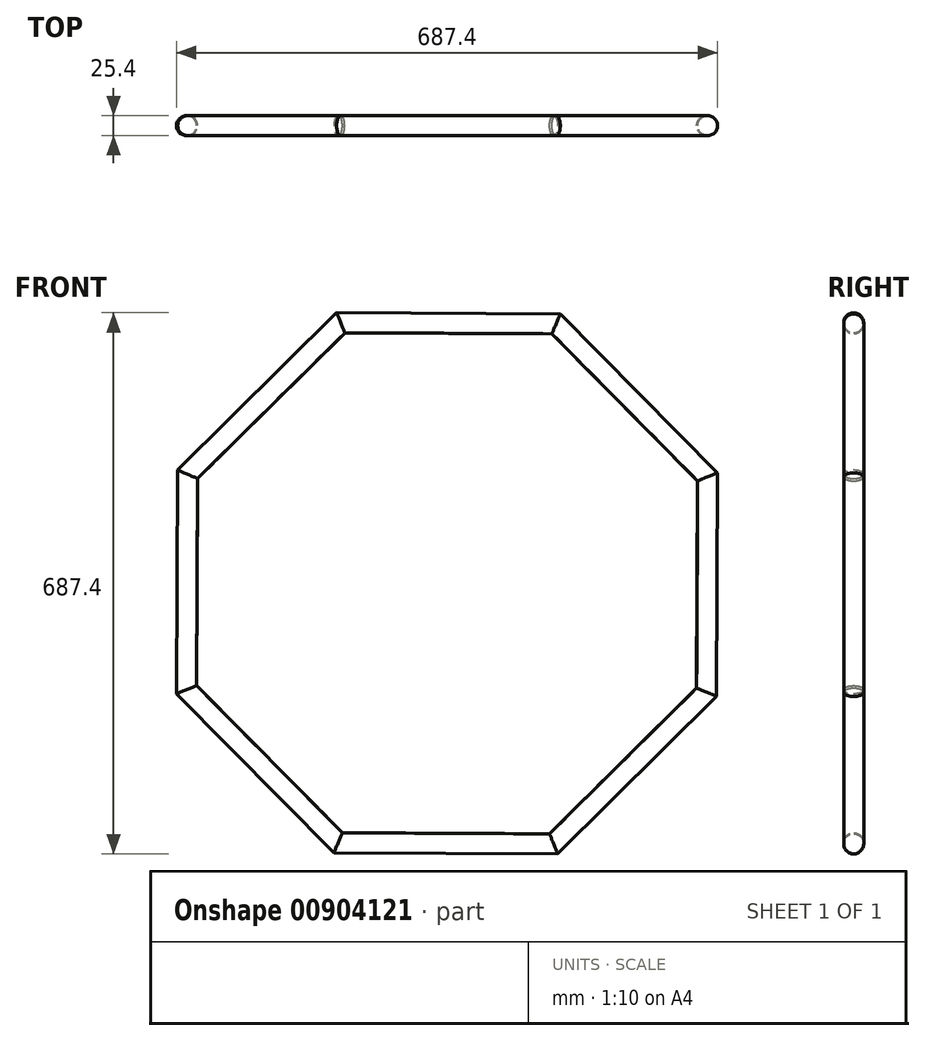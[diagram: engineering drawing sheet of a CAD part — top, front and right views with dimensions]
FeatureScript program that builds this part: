
annotation { "Feature Type Name" : "Feature", "Feature Type Description" : "" }
export const myFeature = defineFeature(function(context is Context, id is Id, definition is map)
    precondition{}
    {
        {
            var Q0;
            Q0=qCreatedBy(makeId("Front.planeOp"),FACE);
            var sketch = newSketch(context, id + "F0", { "sketchPlane" : qUnion([Q0])});
            skLineSegment(sketch, "E0.bottom", {"start": v(304.8, 304.8) * mm, "end": v(-304.8, 304.8) * mm});
            skLineSegment(sketch, "E0.top", {"start": v(304.8, -304.8) * mm, "end": v(-304.8, -304.8) * mm});
            skLineSegment(sketch, "E0.left", {"start": v(304.8, 304.8) * mm, "end": v(304.8, -304.8) * mm});
            skLineSegment(sketch, "E0.right", {"start": v(-304.8, 304.8) * mm, "end": v(-304.8, -304.8) * mm});
            skPoint(sketch, "E0.middle", {"position": v(0, 0) * mm});
            skCircle(sketch, "E1.cCircle", {"center": v(0, 0) * mm, "radius": 459.9 * mm, "construction": true});
            skLineSegment(sketch, "E1.0", {"start": v(460.98, 187.9) * mm, "end": v(458.82, -193.1) * mm});
            skLineSegment(sketch, "E1.1", {"start": v(458.82, -193.1) * mm, "end": v(187.9, -460.98) * mm});
            skLineSegment(sketch, "E1.2", {"start": v(187.9, -460.98) * mm, "end": v(-193.1, -458.82) * mm});
            skLineSegment(sketch, "E1.3", {"start": v(-193.1, -458.82) * mm, "end": v(-460.98, -187.9) * mm});
            skLineSegment(sketch, "E1.4", {"start": v(-460.98, -187.9) * mm, "end": v(-458.82, 193.1) * mm});
            skLineSegment(sketch, "E1.5", {"start": v(-458.82, 193.1) * mm, "end": v(-187.9, 460.98) * mm});
            skLineSegment(sketch, "E1.6", {"start": v(-187.9, 460.98) * mm, "end": v(193.1, 458.82) * mm});
            skLineSegment(sketch, "E1.7", {"start": v(193.1, 458.82) * mm, "end": v(460.98, 187.9) * mm});
            skPoint(sketch, "E1.0.midPoint", {"position": v(459.9, -2.6) * mm});
            skSolve(sketch);
        }
        {
            var Q0;
            Q0=sQuery(id+"F0.wireOp",EDGE,"E1.0");
            cPlane(context, id + "F1", {"entities" : qUnion([Q0]), "cplaneType" : CPlaneType.LINE_ANGLE, "offset" : 25.4 * mm, "angle" : 0 * degree, "width" : 152.4 * mm, "height" : 152.4 * mm});
        }
        {
            var Q0;
            Q0=qCreatedBy(id+"F1.planeOp",FACE);
            var sketch = newSketch(context, id + "F2", { "sketchPlane" : qUnion([Q0])});
            skLineSegment(sketch, "E2.bottom", {"start": v(-113.95, 32.5) * mm, "end": v(-50.67, 32.5) * mm});
            skLineSegment(sketch, "E2.top", {"start": v(-113.95, 77.91) * mm, "end": v(-50.67, 77.91) * mm});
            skLineSegment(sketch, "E2.left", {"start": v(-113.95, 32.5) * mm, "end": v(-113.95, 77.91) * mm});
            skLineSegment(sketch, "E2.right", {"start": v(-50.67, 32.5) * mm, "end": v(-50.67, 77.91) * mm});
            skPoint(sketch, "E2.middle", {"position": v(-82.31, 55.2) * mm});
            skSolve(sketch);
        }
        {
            var Q0;
            Q0=sQuery(id+"F2.wireOp",EDGE,"E2.top");
            cPlane(context, id + "F3", {"entities" : qUnion([Q0]), "cplaneType" : CPlaneType.LINE_ANGLE, "offset" : 25.4 * mm, "angle" : 0 * degree, "width" : 152.4 * mm, "height" : 152.4 * mm});
        }
        {
            var Q0;
            Q0=qCreatedBy(id+"F3.planeOp",FACE);
            var sketch = newSketch(context, id + "F4", { "sketchPlane" : qUnion([Q0])});
            skCircle(sketch, "E3", {"center": v(431.04, 0) * mm, "radius": 12.7 * mm});
            skSolve(sketch);
        }
        {
            var Q0;
            Q0=qCreatedBy(makeId("Front.planeOp"),FACE);
            cPlane(context, id + "F5", {"entities" : qUnion([Q0]), "cplaneType" : CPlaneType.OFFSET, "offset" : 203.2 * mm, "oppositeDirection" : true, "width" : 152.4 * mm, "height" : 152.4 * mm});
        }
        {
            var Q0;
            Q0=qCreatedBy(id+"F5.planeOp",FACE);
            var sketch = newSketch(context, id + "F6", { "sketchPlane" : qUnion([Q0])});
            skCircle(sketch, "E4.cCircle", {"center": v(0, 0) * mm, "radius": 329.13 * mm, "construction": true});
            skLineSegment(sketch, "E4.0", {"start": v(329.78, 134.73) * mm, "end": v(328.46, -137.92) * mm});
            skLineSegment(sketch, "E4.1", {"start": v(328.46, -137.92) * mm, "end": v(134.73, -329.78) * mm});
            skLineSegment(sketch, "E4.2", {"start": v(134.73, -329.78) * mm, "end": v(-137.92, -328.46) * mm});
            skLineSegment(sketch, "E4.3", {"start": v(-137.92, -328.46) * mm, "end": v(-329.78, -134.73) * mm});
            skLineSegment(sketch, "E4.4", {"start": v(-329.78, -134.73) * mm, "end": v(-328.46, 137.92) * mm});
            skLineSegment(sketch, "E4.5", {"start": v(-328.46, 137.92) * mm, "end": v(-134.73, 329.78) * mm});
            skLineSegment(sketch, "E4.6", {"start": v(-134.73, 329.78) * mm, "end": v(137.92, 328.46) * mm});
            skLineSegment(sketch, "E4.7", {"start": v(137.92, 328.46) * mm, "end": v(329.78, 134.73) * mm});
            skPoint(sketch, "E4.0.midPoint", {"position": v(329.12, -1.6) * mm});
            skSolve(sketch);
        }
        {
            var Q0;
            Q0=sQuery(id+"F6.wireOp",EDGE,"E4.4");
            cPlane(context, id + "F7", {"entities" : qUnion([Q0]), "cplaneType" : CPlaneType.LINE_ANGLE, "offset" : 25.4 * mm, "angle" : 0 * degree, "width" : 152.4 * mm, "height" : 152.4 * mm});
        }
        {
            var Q0;
            Q0=qCreatedBy(id+"F7.planeOp",FACE);
            var sketch = newSketch(context, id + "F8", { "sketchPlane" : qUnion([Q0])});
            skLineSegment(sketch, "E5.bottom", {"start": v(203.26, 9.92) * mm, "end": v(384.59, 9.92) * mm});
            skLineSegment(sketch, "E5.top", {"start": v(203.26, 110.23) * mm, "end": v(384.59, 110.23) * mm});
            skLineSegment(sketch, "E5.left", {"start": v(203.26, 9.92) * mm, "end": v(203.26, 110.23) * mm});
            skLineSegment(sketch, "E5.right", {"start": v(384.59, 9.92) * mm, "end": v(384.59, 110.23) * mm});
            skPoint(sketch, "E5.middle", {"position": v(293.93, 60.08) * mm});
            skSolve(sketch);
        }
        {
            var Q0;
            Q0=sQuery(id+"F8.wireOp",EDGE,"E5.top");
            cPlane(context, id + "F9", {"entities" : qUnion([Q0]), "cplaneType" : CPlaneType.LINE_ANGLE, "offset" : 25.4 * mm, "angle" : 0 * degree, "width" : 152.4 * mm, "height" : 152.4 * mm});
        }
        {
            var Q0;
            Q0=qCreatedBy(id+"F9.planeOp",FACE);
            var sketch = newSketch(context, id + "F10", { "sketchPlane" : qUnion([Q0])});
            skCircle(sketch, "E6", {"center": v(-329.78, 203.2) * mm, "radius": 12.7 * mm});
            skSolve(sketch);
        }
        {
            var Q0;
            Q0 = qSketchRegion(id + "F10", true);
            var Q1;
            Q1=sQuery(id+"F6.wireOp",EDGE,"E4.7");
            var Q2;
            Q2=sQuery(id+"F6.wireOp",EDGE,"E4.6");
            var Q3;
            Q3=sQuery(id+"F6.wireOp",EDGE,"E4.5");
            var Q4;
            Q4=sQuery(id+"F6.wireOp",EDGE,"E4.4");
            var Q5;
            Q5=sQuery(id+"F6.wireOp",EDGE,"E4.3");
            var Q6;
            Q6=sQuery(id+"F6.wireOp",EDGE,"E4.2");
            var Q7;
            Q7=sQuery(id+"F6.wireOp",EDGE,"E4.1");
            var Q8;
            Q8=sQuery(id+"F6.wireOp",EDGE,"E4.0");
            sweep(context, id + "F11", {"profiles" : qUnion([Q0]), "path" : qUnion([Q1, Q2, Q3, Q4, Q5, Q6, Q7, Q8])});
        }
        {
            var Q0;
            Q0=sQuery(id+"F0.wireOp",VERTEX,"E1.6.end");
            var Q1;
            Q1=sQuery(id+"F0.wireOp",VERTEX,"E1.5.end");
            var Q2;
            Q2=sQuery(id+"F6.wireOp",VERTEX,"E4.6.end");
            cPlane(context, id + "F12", {"entities" : qUnion([Q0, Q1, Q2]), "cplaneType" : CPlaneType.THREE_POINT, "offset" : 25.4 * mm, "width" : 152.4 * mm, "height" : 152.4 * mm});
        }
        {
            var Q0;
            Q0=qCreatedBy(id+"F12.planeOp",FACE);
            var sketch = newSketch(context, id + "F13", { "sketchPlane" : qUnion([Q0])});
            skLineSegment(sketch, "E7", {"start": v(126.9, -248.02) * mm, "end": v(-108, -248.02) * mm});
            skLineSegment(sketch, "E8", {"start": v(-126.06, -7.53) * mm, "end": v(-113.51, -7.53) * mm});
            skPoint(sketch, "E9.start.orphan", {"position": v(-136.94, 0) * mm});
            skSolve(sketch);
        }
    });
